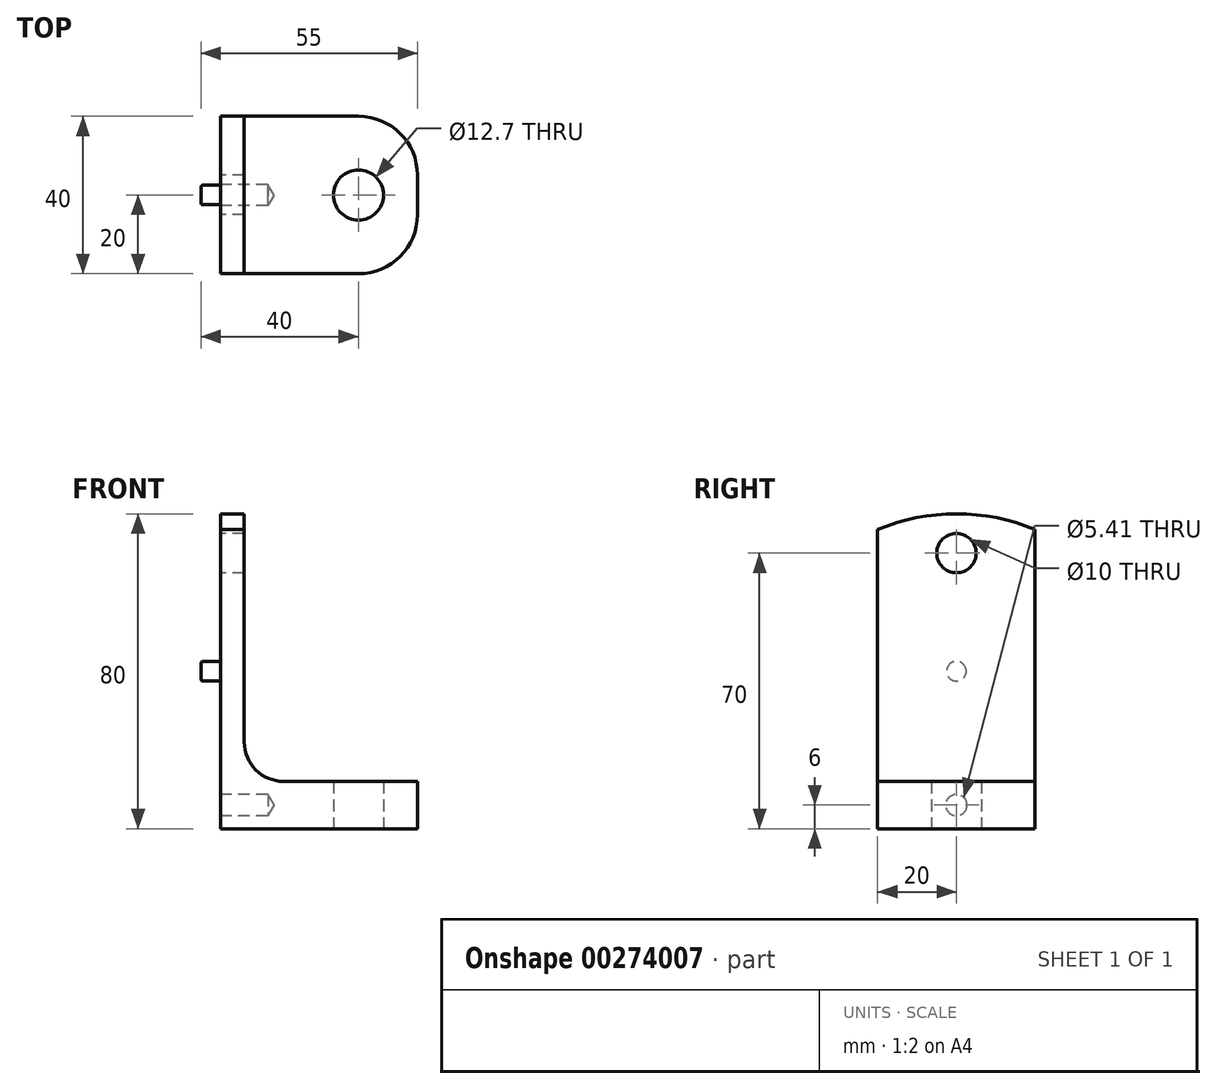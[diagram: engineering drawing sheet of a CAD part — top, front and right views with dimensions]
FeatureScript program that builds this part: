
annotation { "Feature Type Name" : "Feature", "Feature Type Description" : "" }
export const myFeature = defineFeature(function(context is Context, id is Id, definition is map)
    precondition{}
    {
        {
            var Q0;
            Q0=qCreatedBy(makeId("Front.planeOp"),FACE);
            var sketch = newSketch(context, id + "F0", { "sketchPlane" : qUnion([Q0])});
            skLineSegment(sketch, "E0", {"start": v(0, 0) * mm, "end": v(0, 80) * mm});
            skLineSegment(sketch, "E1", {"start": v(0, 80) * mm, "end": v(6, 80) * mm});
            skLineSegment(sketch, "E2", {"start": v(6, 80) * mm, "end": v(6, 12) * mm});
            skLineSegment(sketch, "E3", {"start": v(6, 12) * mm, "end": v(50, 12) * mm});
            skLineSegment(sketch, "E4", {"start": v(50, 12) * mm, "end": v(50, 0) * mm});
            skLineSegment(sketch, "E5", {"start": v(50, 0) * mm, "end": v(0, 0) * mm});
            skSolve(sketch);
        }
        {
            var Q0;
            Q0=qSketchRegion(id+"F0",true);
            extrude(context, id + "F1", {"entities" : qUnion([Q0]), "endBound" : BoundingType.SYMMETRIC, "depth" : 40 * mm});
        }
        {
            var Q0;
            Q0=makeQuery(id+"F1.opExtrude","SWEPT_EDGE",EDGE,{"disambiguationData":[OSD([sQuery(id+"F0.wireOp",EDGE,"E2"),sQuery(id+"F0.wireOp",EDGE,"E3")])]});
            fillet(context, id + "F2", {"entities" : qUnion([Q0]), "radius" : 10 * mm, "tangentPropagation" : true, "allowEdgeOverflow" : false});
        }
        {
            var Q0;
            Q0=makeQuery(id+"F1.opExtrude","SWEPT_FACE",FACE,{"disambiguationData":[OSD([sQuery(id+"F0.wireOp",EDGE,"E5")])]});
            var sketch = newSketch(context, id + "F3", { "sketchPlane" : qUnion([Q0])});
            skCircle(sketch, "E6", {"center": v(35, 0) * mm, "radius": 6.35 * mm});
            skSolve(sketch);
        }
        {
            var Q0;
            Q0=qSketchRegion(id+"F3",true);
            extrude(context, id + "F4", {"entities" : qUnion([Q0]), "operationType" : NewBodyOperationType.REMOVE, "endBound" : BoundingType.THROUGH_ALL, "oppositeDirection" : true, "depth" : 25 * mm});
        }
        {
            var Q0;
            Q0=makeQuery(id+"F1.opExtrude","SWEPT_FACE",FACE,{"disambiguationData":[OSD([sQuery(id+"F0.wireOp",EDGE,"E0")])]});
            var sketch = newSketch(context, id + "F5", { "sketchPlane" : qUnion([Q0])});
            skPoint(sketch, "E7", {"position": v(0, 6) * mm});
            skSolve(sketch);
        }
        {
            var Q0;
            Q0=sQuery(id+"F5.wireOp",VERTEX,"E7");
            var Q1;
            Q1=makeQuery(id+"F1.opExtrude","SWEPT_BODY",BODY,{"disambiguationData":[OSD([sQuery(id+"F0.wireOp",EDGE,"E0"),sQuery(id+"F0.wireOp",EDGE,"E1"),sQuery(id+"F0.wireOp",EDGE,"E2"),sQuery(id+"F0.wireOp",EDGE,"E3"),sQuery(id+"F0.wireOp",EDGE,"E4"),sQuery(id+"F0.wireOp",EDGE,"E5")])]});
            hole(context, id + "F6", {"style" : HoleStyle.SIMPLE, "endStyle" : HoleEndStyle.BLIND, "standardTappedOrClearance" : lookupTablePath({ "standard" : "ANSI", "engagement" : "75%", "pitch" : "28 tpi", "size" : "1/4", "type" : "Tapped" }), "standardBlindInLast" : lookupTablePath({ "standard" : "ANSI", "engagement" : "75%", "pitch" : "28 tpi", "size" : "1/4", "type" : "Tapped" }), "holeDiameter" : 5.4 * mm, "holeDepth" : 12 * mm, "locations" : qUnion([Q0]), "scope" : qUnion([Q1]), "majorDiameter" : 6.35 * mm});
        }
        {
            var Q0;
            Q0=makeQuery(id+"F1.opExtrude","SWEPT_FACE",FACE,{"disambiguationData":[OSD([sQuery(id+"F0.wireOp",EDGE,"E0")])]});
            var sketch = newSketch(context, id + "F7", { "sketchPlane" : qUnion([Q0])});
            skArc(sketch, "E8", {"start": v(20, 76) * mm, "mid": v(0, 80) * mm, "end": v(-20, 76) * mm});
            skLineSegment(sketch, "E9.0", {"start": v(20, 80) * mm, "end": v(-20, 80) * mm});
            skLineSegment(sketch, "E10.0", {"start": v(-20, 76) * mm, "end": v(-20, 80) * mm});
            skLineSegment(sketch, "E10.1", {"start": v(20, 76) * mm, "end": v(20, 80) * mm});
            skPoint(sketch, "E11.orphan", {"position": v(20, 0) * mm});
            skPoint(sketch, "E12.orphan", {"position": v(-20, 0) * mm});
            skCircle(sketch, "E13", {"center": v(0, 70) * mm, "radius": 5 * mm});
            skSolve(sketch);
        }
        {
            var Q0;
            Q0=qSketchRegion(id+"F7",true);
            extrude(context, id + "F8", {"entities" : qUnion([Q0]), "operationType" : NewBodyOperationType.REMOVE, "endBound" : BoundingType.THROUGH_ALL, "oppositeDirection" : true, "depth" : 25 * mm});
        }
        {
            var Q0;
            Q0=makeQuery(id+"F1.opExtrude","SWEPT_FACE",FACE,{"disambiguationData":[OSD([sQuery(id+"F0.wireOp",EDGE,"E0")])]});
            var sketch = newSketch(context, id + "F9", { "sketchPlane" : qUnion([Q0])});
            skCircle(sketch, "E14", {"center": v(0, 40) * mm, "radius": 2.5 * mm});
            skSolve(sketch);
        }
        {
            var Q0;
            Q0=qSketchRegion(id+"F9",true);
            extrude(context, id + "F10", {"entities" : qUnion([Q0]), "operationType" : NewBodyOperationType.ADD, "depth" : 5 * mm});
        }
        {
            var Q0;
            Q0=makeQuery(id+"F10.opExtrude","CAP_EDGE",EDGE,{"disambiguationData":[OSD([sQuery(id+"F9.wireOp",EDGE,"E14")])],"isStart":true});
            var Q1;
            Q1=makeQuery(id+"F10.opExtrude","CAP_EDGE",EDGE,{"disambiguationData":[OSD([sQuery(id+"F9.wireOp",EDGE,"E14")])],"isStart":false});
            fillet(context, id + "F11", {"entities" : qUnion([Q0, Q1]), "radius" : 0.5 * mm, "tangentPropagation" : true, "allowEdgeOverflow" : false});
        }
        {
            var Q0;
            Q0=makeQuery(id+"F1.opExtrude","CAP_EDGE",EDGE,{"disambiguationData":[OSD([sQuery(id+"F0.wireOp",EDGE,"E4")])],"isStart":false});
            var Q1;
            Q1=makeQuery(id+"F1.opExtrude","CAP_EDGE",EDGE,{"disambiguationData":[OSD([sQuery(id+"F0.wireOp",EDGE,"E4")])],"isStart":true});
            fillet(context, id + "F12", {"entities" : qUnion([Q0, Q1]), "radius" : 15 * mm, "tangentPropagation" : true, "allowEdgeOverflow" : false});
        }
    });
